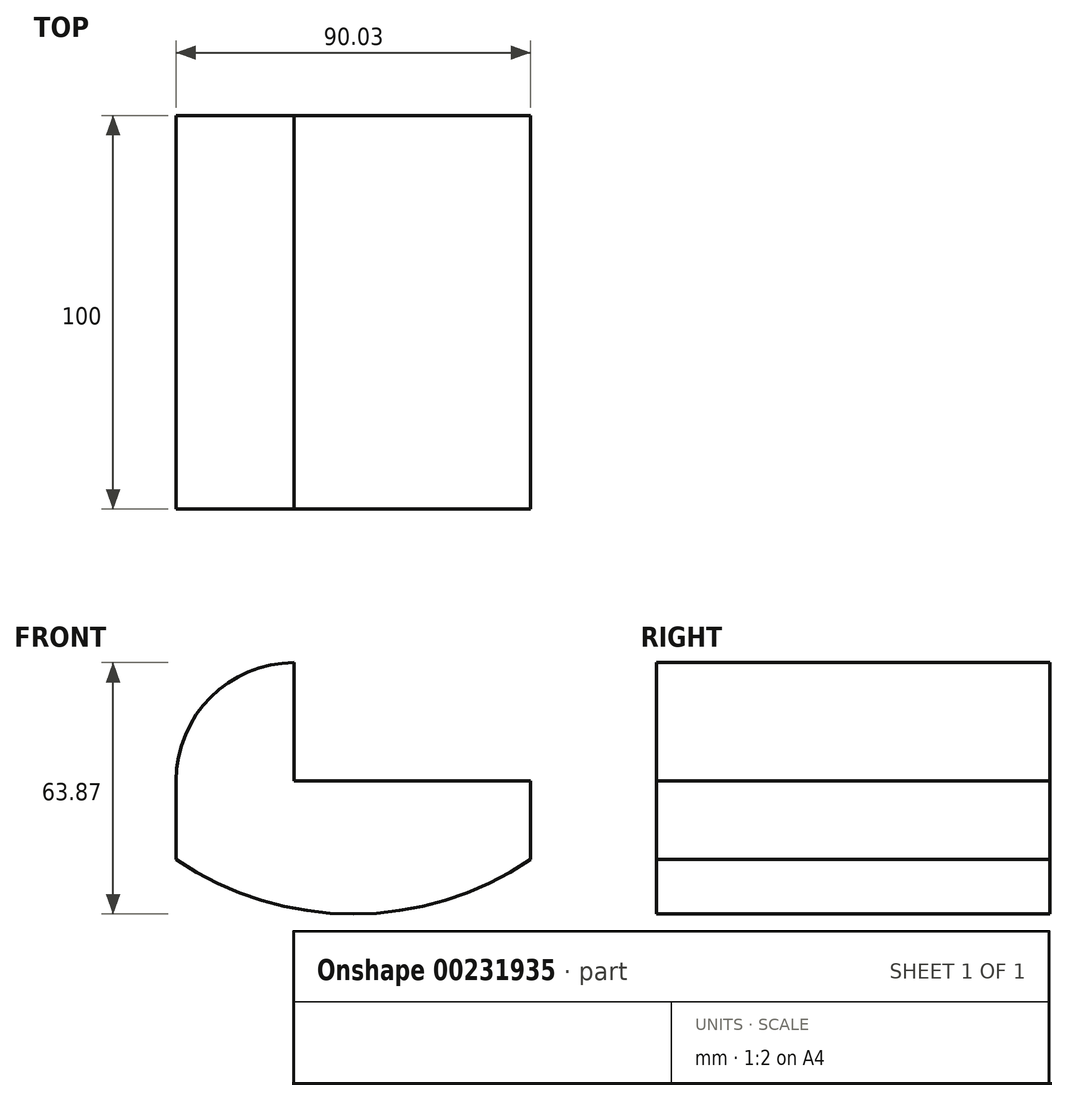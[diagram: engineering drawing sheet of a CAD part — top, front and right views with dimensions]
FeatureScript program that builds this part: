
annotation { "Feature Type Name" : "Feature", "Feature Type Description" : "" }
export const myFeature = defineFeature(function(context is Context, id is Id, definition is map)
    precondition{}
    {
        {
            var Q0;
            Q0=qCreatedBy(makeId("Front.planeOp"),FACE);
            var sketch = newSketch(context, id + "F0", { "sketchPlane" : qUnion([Q0])});
            skLineSegment(sketch, "E0", {"start": v(32.68, -22.62) * mm, "end": v(32.68, -2.62) * mm});
            skLineSegment(sketch, "E1", {"start": v(32.68, -2.62) * mm, "end": v(-27.35, -2.62) * mm});
            skLineSegment(sketch, "E2", {"start": v(-27.35, -2.62) * mm, "end": v(-27.35, 27.38) * mm});
            skArc(sketch, "E3", {"start": v(-27.35, 27.38) * mm, "mid": v(-48.57, 18.6) * mm, "end": v(-57.35, -2.62) * mm});
            skLineSegment(sketch, "E4", {"start": v(-57.35, -2.62) * mm, "end": v(-57.35, -22.62) * mm});
            skArc(sketch, "E5", {"start": v(-57.35, -22.62) * mm, "mid": v(-12.34, -36.5) * mm, "end": v(32.68, -22.62) * mm});
            skSolve(sketch);
        }
        {
            var Q0;
            Q0 = qSketchRegion(id + "F0", true);
            extrude(context, id + "F1", {"entities" : qUnion([Q0]), "depth" : 100 * mm});
        }
    });
